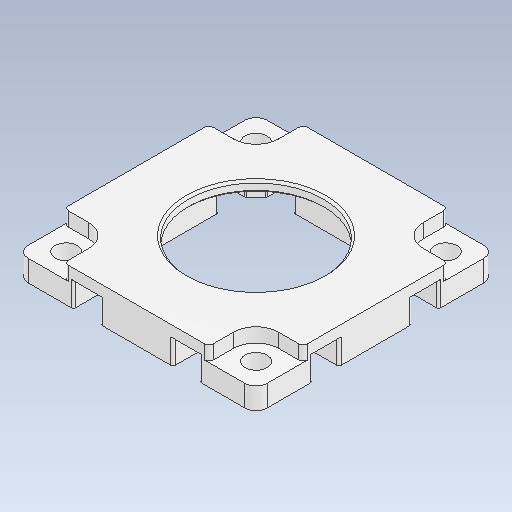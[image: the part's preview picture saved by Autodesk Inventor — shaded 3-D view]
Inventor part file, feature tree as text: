
AUTODESK INVENTOR PART (.ipt)
format: ipt  version: 2020 (Build 240168000, 168)  size: 181,248 bytes
history: native  units: in
note: dims shown in document units (in); Inventor stores cm internally (conversion verified against a paired STEP export)
features: fillet x1
ambient origin geometry x8: Origin, YZ Plane, XZ Plane, XY Plane, X Axis, Y Axis, Z Axis, Center Point
bodies: Solid1 (feature_tree)
feature tree (1):
  fillet  "Fillet4"  [1 undecoded]
note: 1 required parameter value undecoded (feature->parameter linkage not recoverable at this tier; creation-order binding heuristic only, values carry confidence <= 0.55)
